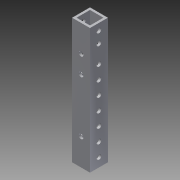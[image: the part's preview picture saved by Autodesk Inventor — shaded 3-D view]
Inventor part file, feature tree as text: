
AUTODESK INVENTOR PART (.ipt)
format: ipt  version: 2014 SP1 (Build 180222100, 222)  size: 146,432 bytes
history: native  units: in
note: dims shown in document units (in); Inventor stores cm internally (conversion verified against a paired STEP export)
features: extrude x4, sketch x4, reference x2
ambient origin geometry x8: Origin, YZ Plane, XZ Plane, XY Plane, X Axis, Y Axis, Z Axis, Center Point
bodies: Solid1 (feature_tree)
feature tree (10):
  extrude  "Extrusion1"  Depth=1.0in
  extrude  "Extrusion2"  Depth=7.0in TaperAngle=0.0deg
  extrude  "Extrusion3"  Depth=1.0in
  extrude  "Extrusion4"  Depth=1.0in
  sketch  "Sketch1"  dims[d0=1.0in d1=1.0in]
  sketch  "Sketch2"  dims[d2=0.125in d3=7.0in d4=0.0in]
  reference  "Reference5"
  reference  "Reference6"
  sketch  "Sketch3"  dims[d6=1.0in d7=0.0in d16=0.26in]
  sketch  "Sketch4"  dims[d17=0.26in d18=4.25in d19=0.26in d20=0.5in d21=0.5in d22=0.26in d23=1.0in d24=2.3622in d26=0.75in d27=0.3937in d29=1.0in d31=1.0in d32=0.0in d33=0.26in d35=1.5in d36=1.9685in d38=1.0in d39=0.3937in d41=1.0in d43=1.0in d44=0.0in]
